# Revit family: Drinking_Fountain_Bottle_Filler-Murdock-M-DFBF_Series
name_source: partatom
category: Plumbing Fixtures
revit_build: Autodesk Revit 2018 (Build: 20170223_1515(x64)
units: mm (PartAtom-declared; Revit-internal decimal feet)

## family parameters
Cut with Voids When Loaded = No
Host = Face
OmniClass Number = 23.65.70.14.11
OmniClass Title = Drinking Fountains/Coolers
Part Type = Normal
Room Calculation Point = No
Round Connector Dimension = Use Diameter
Shared = Yes

## types (3) — shared parameters
-BAT Battery Operated Sensors = No
-EG Enviro-Glaze, Specify Color:(Drinking Fountain, Bottle Filler, Trap Cover) = No
-WF1 1500-Gallon Capacity, NSF 42+53, 1-Micron Lead Reduction Filter = No
-WF3 3000-Gallon Capacity, NSF 42+53, 1-Micron Lead Reduction Filte = No
A9100080 - A Remote Chiller, 8 Gallons Per Hour = No
ADA Compliant = Yes
Assembly Code = D2010800
Body Material = Stainless Steel-Murdock-Type 304-#4 Satin
CW Connection = Yes
CWFU = 1.5
Cold Water Connection Diameter = 3/8"
Cold Water Connection Height = 21 1/2"
Cold Water Connection Width = 2 5/8"
Default Elevation = 31 3/4"
Description = Heavy duty, barrier free, wall mounted drinking fountain with concealed sensor and bottle filler with sensor operation
Fill Rate = 1.0 GPM (3.8 LPM)
Flow Rate = 0.3 GPM
HW Connection = No
Height = 49 3/4"
IAPMO Compliance = Unit is certified to ANSI A117.1, Public Law111-380(NO-LEAD),CHSC116875and NSF/ANSI 61, Section
Installation Type = Wall Mounted
Length = 24 3/8"
Manufacturer = Murdock Manufacturing
Model = M-DFBF
Power = 120V AC/ 9.0 VDC
Revised Date = 06/25/2021
Strainer Material = Metal-Murdock-Stainless Steel
URL = https://www.murdockmfg.com
Vent Connection = No
WFU = 2
Waste Connection = Yes
Waste Connection Diameter = 1 1/2"
Waste Connection Height = 25 1/4"
Width = 21"
zero-valued in all types: HWFU

## per-type parameters (varying)
| type | Bubbler Material | Type Comments |
| M-DFBF-LR | Stainless Steel-Murdock-Ligature Resistant White | Ligature Resistant Stn Stl Bubbler |
| M-DFBF-F | Stainless Steel-Murdock-Grey | Gray Flexible Code Bubbler |
| M-DFBF-S | Metal-Murdock-Stainless Steel | Satin Stainless Code Bubbler |

## geometry (parser evidence)
native form markers: Sweep x5
no freeform markers — native parametric forms only
